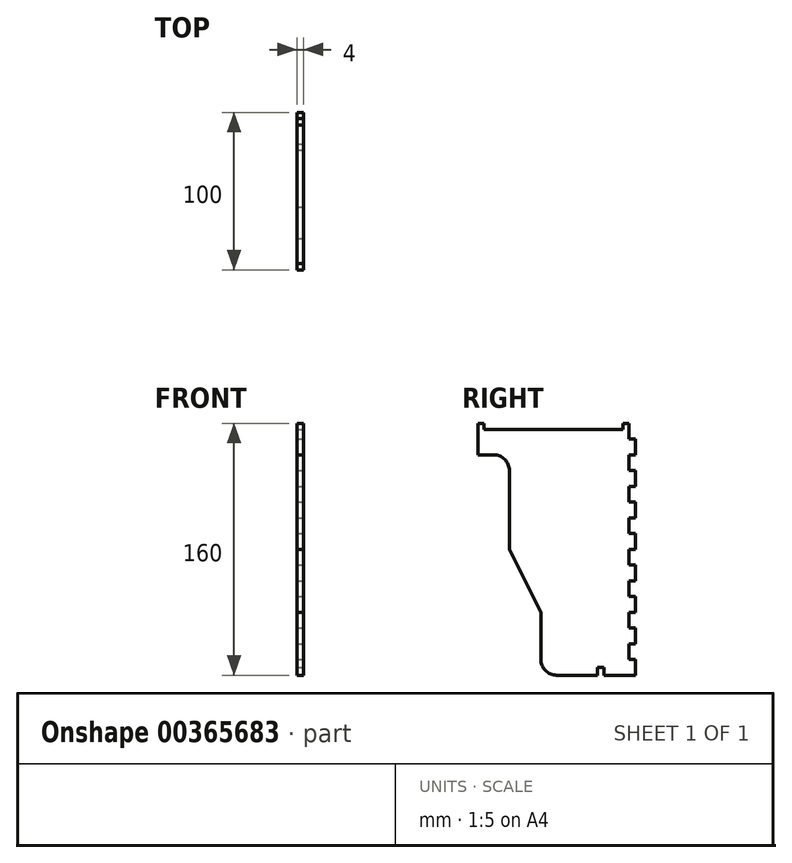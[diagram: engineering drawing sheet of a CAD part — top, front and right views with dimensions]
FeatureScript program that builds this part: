
annotation { "Feature Type Name" : "Feature", "Feature Type Description" : "" }
export const myFeature = defineFeature(function(context is Context, id is Id, definition is map)
    precondition{}
    {
        {
            var Q0;
            Q0=qCreatedBy(makeId("Right.planeOp"),FACE);
            var sketch = newSketch(context, id + "F0", { "sketchPlane" : qUnion([Q0])});
            skLineSegment(sketch, "E0.bottom", {"start": v(0, 0) * mm, "end": v(100, 0) * mm});
            skLineSegment(sketch, "E0.top", {"start": v(0, 160) * mm, "end": v(100, 160) * mm});
            skLineSegment(sketch, "E0.left", {"start": v(0, 0) * mm, "end": v(0, 160) * mm});
            skLineSegment(sketch, "E0.right", {"start": v(100, 0) * mm, "end": v(100, 160) * mm});
            skSolve(sketch);
        }
        {
            var Q0;
            Q0 = qSketchRegion(id + "F0", true);
            extrude(context, id + "F1", {"entities" : qUnion([Q0]), "depth" : 4 * mm});
        }
        {
            var Q0;
            Q0=makeQuery(id+"F1.opExtrude","CAP_FACE",FACE,{"disambiguationData":[OSD([sQuery(id+"F0.wireOp",EDGE,"E0.bottom"),sQuery(id+"F0.wireOp",EDGE,"E0.top"),sQuery(id+"F0.wireOp",EDGE,"E0.left"),sQuery(id+"F0.wireOp",EDGE,"E0.right")])],"isStart":false});
            var sketch = newSketch(context, id + "F2", { "sketchPlane" : qUnion([Q0])});
            skLineSegment(sketch, "E1.bottom", {"start": v(100, 160) * mm, "end": v(96, 160) * mm});
            skLineSegment(sketch, "E1.top", {"start": v(100, 150) * mm, "end": v(96, 150) * mm});
            skLineSegment(sketch, "E1.left", {"start": v(100, 160) * mm, "end": v(100, 150) * mm});
            skLineSegment(sketch, "E1.right", {"start": v(96, 160) * mm, "end": v(96, 150) * mm});
            skLineSegment(sketch, "E2.0.1.0", {"start": v(100, 140) * mm, "end": v(96, 140) * mm});
            skLineSegment(sketch, "E2.0.1.1", {"start": v(100, 130) * mm, "end": v(96, 130) * mm});
            skLineSegment(sketch, "E2.0.1.2", {"start": v(100, 140) * mm, "end": v(100, 130) * mm});
            skLineSegment(sketch, "E2.0.1.3", {"start": v(96, 140) * mm, "end": v(96, 130) * mm});
            skLineSegment(sketch, "E2.0.2.0", {"start": v(100, 120) * mm, "end": v(96, 120) * mm});
            skLineSegment(sketch, "E2.0.2.1", {"start": v(100, 110) * mm, "end": v(96, 110) * mm});
            skLineSegment(sketch, "E2.0.2.2", {"start": v(100, 120) * mm, "end": v(100, 110) * mm});
            skLineSegment(sketch, "E2.0.2.3", {"start": v(96, 120) * mm, "end": v(96, 110) * mm});
            skLineSegment(sketch, "E2.0.3.0", {"start": v(100, 100) * mm, "end": v(96, 100) * mm});
            skLineSegment(sketch, "E2.0.3.1", {"start": v(100, 90) * mm, "end": v(96, 90) * mm});
            skLineSegment(sketch, "E2.0.3.2", {"start": v(100, 100) * mm, "end": v(100, 90) * mm});
            skLineSegment(sketch, "E2.0.3.3", {"start": v(96, 100) * mm, "end": v(96, 90) * mm});
            skLineSegment(sketch, "E2.0.4.0", {"start": v(100, 80) * mm, "end": v(96, 80) * mm});
            skLineSegment(sketch, "E2.0.4.1", {"start": v(100, 70) * mm, "end": v(96, 70) * mm});
            skLineSegment(sketch, "E2.0.4.2", {"start": v(100, 80) * mm, "end": v(100, 70) * mm});
            skLineSegment(sketch, "E2.0.4.3", {"start": v(96, 80) * mm, "end": v(96, 70) * mm});
            skLineSegment(sketch, "E2.0.5.0", {"start": v(100, 60) * mm, "end": v(96, 60) * mm});
            skLineSegment(sketch, "E2.0.5.1", {"start": v(100, 50) * mm, "end": v(96, 50) * mm});
            skLineSegment(sketch, "E2.0.5.2", {"start": v(100, 60) * mm, "end": v(100, 50) * mm});
            skLineSegment(sketch, "E2.0.5.3", {"start": v(96, 60) * mm, "end": v(96, 50) * mm});
            skLineSegment(sketch, "E2.0.6.0", {"start": v(100, 40) * mm, "end": v(96, 40) * mm});
            skLineSegment(sketch, "E2.0.6.1", {"start": v(100, 30) * mm, "end": v(96, 30) * mm});
            skLineSegment(sketch, "E2.0.6.2", {"start": v(100, 40) * mm, "end": v(100, 30) * mm});
            skLineSegment(sketch, "E2.0.6.3", {"start": v(96, 40) * mm, "end": v(96, 30) * mm});
            skLineSegment(sketch, "E2.0.7.0", {"start": v(100, 20) * mm, "end": v(96, 20) * mm});
            skLineSegment(sketch, "E2.0.7.1", {"start": v(100, 10) * mm, "end": v(96, 10) * mm});
            skLineSegment(sketch, "E2.0.7.2", {"start": v(100, 20) * mm, "end": v(100, 10) * mm});
            skLineSegment(sketch, "E2.0.7.3", {"start": v(96, 20) * mm, "end": v(96, 10) * mm});
            skLineSegment(sketch, "E2.direction1", {"start": v(96, 150) * mm, "end": v(100, 150) * mm, "construction": true});
            skLineSegment(sketch, "E2.direction2", {"start": v(96, 150) * mm, "end": v(96, 130) * mm, "construction": true});
            skSolve(sketch);
        }
        {
            var Q0;
            Q0 = qSketchRegion(id + "F2", true);
            extrude(context, id + "F3", {"entities" : qUnion([Q0]), "operationType" : NewBodyOperationType.REMOVE, "endBound" : BoundingType.UP_TO_NEXT, "oppositeDirection" : true, "depth" : 25 * mm});
        }
        {
            var Q0;
            Q0=makeQuery(id+"F1.opExtrude","CAP_FACE",FACE,{"disambiguationData":[OSD([sQuery(id+"F0.wireOp",EDGE,"E0.bottom"),sQuery(id+"F0.wireOp",EDGE,"E0.top"),sQuery(id+"F0.wireOp",EDGE,"E0.left"),sQuery(id+"F0.wireOp",EDGE,"E0.right")])],"isStart":false});
            var sketch = newSketch(context, id + "F4", { "sketchPlane" : qUnion([Q0])});
            skLineSegment(sketch, "E3.bottom", {"start": v(80, 0) * mm, "end": v(76, 0) * mm});
            skLineSegment(sketch, "E3.top", {"start": v(80, 5) * mm, "end": v(76, 5) * mm});
            skLineSegment(sketch, "E3.left", {"start": v(80, 0) * mm, "end": v(80, 5) * mm});
            skLineSegment(sketch, "E3.right", {"start": v(76, 0) * mm, "end": v(76, 5) * mm});
            skPoint(sketch, "E4.visualSharp", {"position": v(76, 5) * mm});
            skPoint(sketch, "E5.visualSharp", {"position": v(80, 5) * mm});
            skLineSegment(sketch, "E6.bottom", {"start": v(92, 160) * mm, "end": v(4, 160) * mm});
            skLineSegment(sketch, "E6.top", {"start": v(92, 156) * mm, "end": v(4, 156) * mm});
            skLineSegment(sketch, "E6.left", {"start": v(92, 160) * mm, "end": v(92, 156) * mm});
            skLineSegment(sketch, "E6.right", {"start": v(4, 160) * mm, "end": v(4, 156) * mm});
            skSolve(sketch);
        }
        {
            var Q0;
            Q0 = qSketchRegion(id + "F4", true);
            extrude(context, id + "F5", {"entities" : qUnion([Q0]), "operationType" : NewBodyOperationType.REMOVE, "endBound" : BoundingType.UP_TO_NEXT, "oppositeDirection" : true, "depth" : 25 * mm});
        }
        {
            var Q0;
            Q0=makeQuery(id+"F1.opExtrude","CAP_FACE",FACE,{"disambiguationData":[OSD([sQuery(id+"F0.wireOp",EDGE,"E0.bottom"),sQuery(id+"F0.wireOp",EDGE,"E0.top"),sQuery(id+"F0.wireOp",EDGE,"E0.left"),sQuery(id+"F0.wireOp",EDGE,"E0.right")])],"isStart":false});
            var sketch = newSketch(context, id + "F6", { "sketchPlane" : qUnion([Q0])});
            skLineSegment(sketch, "E7", {"start": v(0, 140) * mm, "end": v(10, 140) * mm});
            skLineSegment(sketch, "E8", {"start": v(20, 130) * mm, "end": v(20, 80) * mm});
            skLineSegment(sketch, "E9", {"start": v(20, 80) * mm, "end": v(40, 40) * mm});
            skLineSegment(sketch, "E10", {"start": v(40, 40) * mm, "end": v(40, 0) * mm});
            skLineSegment(sketch, "E11", {"start": v(0, 140) * mm, "end": v(0, 0) * mm});
            skLineSegment(sketch, "E12", {"start": v(0, 0) * mm, "end": v(40, 0) * mm});
            skPoint(sketch, "E13.visualSharp", {"position": v(20, 140) * mm});
            skArc(sketch, "E13.filletArc", {"start": v(20, 130) * mm, "mid": v(17.07, 137.07) * mm, "end": v(10, 140) * mm});
            skLineSegment(sketch, "E14", {"start": v(40, 0) * mm, "end": v(50, 0) * mm});
            skPoint(sketch, "E15", {"position": v(50, 10) * mm});
            skArc(sketch, "E16", {"start": v(50, 0) * mm, "mid": v(42.93, 2.93) * mm, "end": v(40, 10) * mm});
            skSolve(sketch);
        }
        {
            var Q0;
            Q0 = qSketchRegion(id + "F6", true);
            extrude(context, id + "F7", {"entities" : qUnion([Q0]), "operationType" : NewBodyOperationType.REMOVE, "endBound" : BoundingType.UP_TO_NEXT, "oppositeDirection" : true, "depth" : 25 * mm});
        }
    });
